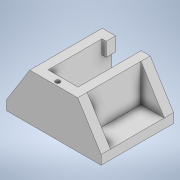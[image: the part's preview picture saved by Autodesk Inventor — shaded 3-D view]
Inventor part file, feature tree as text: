
AUTODESK INVENTOR PART (.ipt)
format: ipt  version: 2020 (Build 240168000, 168)  size: 202,752 bytes
history: native  units: mm
features: sketch x10, extrude x9
ambient origin geometry x8: Origin, YZ Plane, XZ Plane, XY Plane, X Axis, Y Axis, Z Axis, Center Point
bodies: Solid1 (feature_tree)
feature tree (19):
  sketch  "Sketch1"  dims[d0=20.5mm d1=31.0mm]
  extrude  "Extrusion1"  Depth=31.0mm
  extrude  "Extrusion2"  Depth=23.0mm
  extrude  "Extrusion3"  Depth=4.0mm
  extrude  "Extrusion4"  Depth=3.875mm
  extrude  "Extrusion5"  Depth=16.0mm TaperAngle=0.0deg
  extrude  "Extrusion6"  Depth=12.75mm
  extrude  "Extrusion7"  Depth=3.875mm
  extrude  "Extrusion8"  Depth=6.0mm
  extrude  "Extrusion9"  Depth=4.0mm
  sketch  "Sketch2"  dims[d2=20.0mm d3=0.0mm d4=23.0mm]
  sketch  "Sketch3"  dims[d5=12.75mm d6=4.0mm]
  sketch  "Sketch4"  dims[d7=3.875mm d8=3.875mm]
  sketch  "Sketch5"  dims[d9=4.0mm d10=16.0mm d11=0.0mm]
  sketch  "Sketch6"  dims[d12=10.0mm d13=12.75mm]
  sketch  "Sketch8"  dims[d14=4.0mm d15=3.875mm]
  sketch  "Sketch9"  dims[d16=3.875mm d17=6.0mm]
  sketch  "Sketch10"  dims[d18=4.0mm d19=0.0mm d20=1.95mm]
  sketch  "Sketch11"  dims[d21=2.3mm d22=10.25mm d23=10.25mm d24=1.95mm d25=2.3mm d26=10.25mm d27=10.25mm d28=8.0mm d29=0.0mm d30=10.0mm d31=0.0mm d32=10.0mm d33=0.0mm d34=4.0mm d35=0.0mm d36=4.0mm d37=0.0mm d38=11.0mm d39=6.0mm d40=0.0mm]
